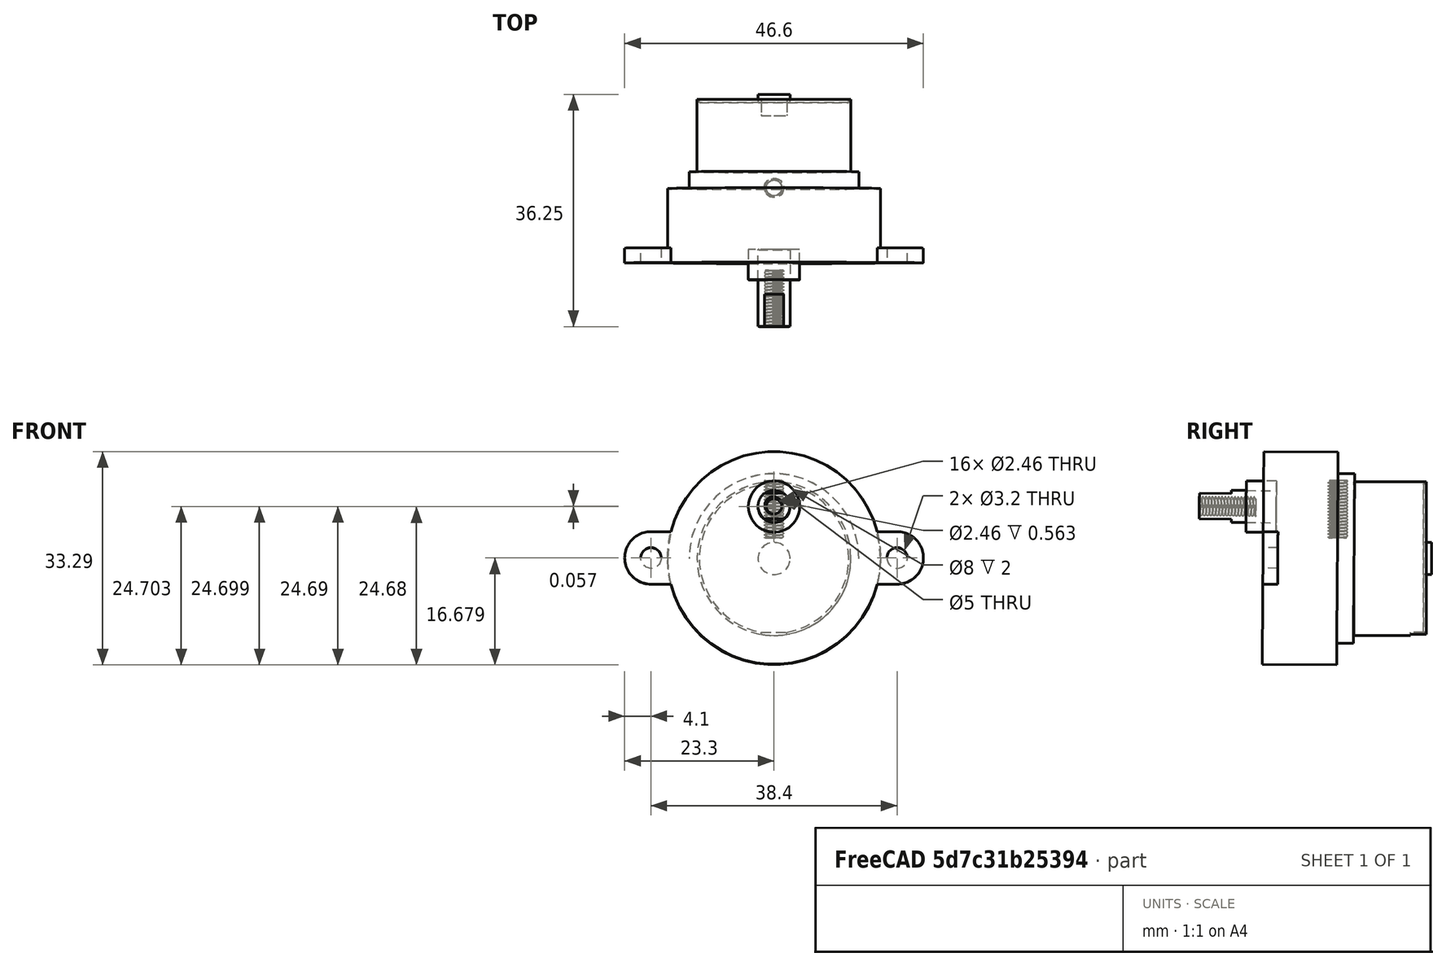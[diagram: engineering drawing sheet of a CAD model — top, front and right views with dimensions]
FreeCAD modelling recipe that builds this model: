
FCSTD DOCUMENT  (FreeCAD 1.0R39319 (Git))
Label: JS30
License: CC0 1.0 Universal
LicenseURL: https://creativecommons.org/publicdomain/zero/1.0/legalcode.txt
objects: Sketcher::SketchObject×11, PartDesign::Pad×6, PartDesign::Pocket×5, PartDesign::Body×4, App::FeaturePython×4, PartDesign::Mirrored×2, Part::FeaturePython×1, PartDesign::Boolean×1, Assembly::JointGroup×1, Assembly::AssemblyObject×1
note: 66 computed .brp shape members not serialized (recipe doc carries the construction recipe); baked Part::Feature solids carry a one-line shape summary decoded from their .brp

FEATURE [Sketcher::SketchObject] Sketch
  ArcFitTolerance = 1e-06
  AttachmentSupport = -> [XZ_Plane]
  FullyConstrained = true
  MakeInternals = false
  MapMode = 5
  Placement = pos=(0,0,0) rot=(1,0,0;1.5708rad)
  sketch-geometry (1):
    g0: Circle CenterX=0 CenterY=0 CenterZ=0 NormalX=0 NormalY=0 NormalZ=1 AngleXU=0 Radius=12
  constraints (2):
    c: Diameter(g0) = 24
    c: Coincident(g0,g-1)
FEATURE [PartDesign::Pad] Pad
  Direction = (0,-1,2e-16)
  Length = 11.3
  Length2 = 10
  Placement = pos=(0,0,0) rot=(1,0,0;1.5708rad)
  Profile = -> Sketch [Edge1]
  ReferenceAxis = -> Sketch [N_Axis]
  Refine = true
  Reversed = true
  Suppressed = false
  Type = 0
FEATURE [Sketcher::SketchObject] Sketch001
  ArcFitTolerance = 1e-06
  AttachmentSupport = -> [Pad]
  FullyConstrained = true
  MakeInternals = false
  MapMode = 5
  Placement = pos=(0,11.3,0) rot=(-1,0,0;1.5708rad)
  sketch-geometry (1):
    g0: Circle CenterX=0 CenterY=0 CenterZ=0 NormalX=0 NormalY=0 NormalZ=1 AngleXU=0 Radius=11.65
  constraints (2):
    c: Diameter(g0) = 23.3
    c: Coincident(g0,g-1)
FEATURE [PartDesign::Pocket] Pocket
  BaseFeature = -> Pad
  Direction = (0,-1,-2e-16)
  Length = 0.5
  Length2 = 5
  Placement = pos=(0,0,0) rot=(1,0,0;1.5708rad)
  Profile = -> Sketch001
  ReferenceAxis = -> Sketch001 [N_Axis]
  Refine = true
  Suppressed = false
  Type = 0
FEATURE [Sketcher::SketchObject] Sketch002
  ArcFitTolerance = 1e-06
  AttachmentSupport = -> [XZ_Plane001]
  FullyConstrained = true
  MakeInternals = false
  MapMode = 5
  Placement = pos=(0,0,0) rot=(1,0,0;1.5708rad)
  sketch-geometry (1):
    g0: Circle CenterX=0 CenterY=0 CenterZ=0 NormalX=0 NormalY=0 NormalZ=1 AngleXU=0 Radius=16.6
  constraints (2):
    c: Diameter(g0) = 33.2
    c: Coincident(g0,g-1)
FEATURE [PartDesign::Pad] Pad001
  Direction = (0,-1,2e-16)
  Length = 14.2
  Length2 = 10
  Placement = pos=(0,0,0) rot=(1,0,0;1.5708rad)
  Profile = -> Sketch002 [Edge1]
  ReferenceAxis = -> Sketch002 [N_Axis]
  Refine = true
  Suppressed = false
  Type = 0
FEATURE [Sketcher::SketchObject] Sketch003
  ArcFitTolerance = 1e-06
  AttachmentSupport = -> [XZ_Plane001]
  ExternalGeometry = -> [Pad001]
  FullyConstrained = true
  MakeInternals = false
  MapMode = 5
  Placement = pos=(0,0,0) rot=(1,0,0;1.5708rad)
  sketch-geometry (2):
    g0: Circle CenterX=0 CenterY=0 CenterZ=0 NormalX=0 NormalY=0 NormalZ=1 AngleXU=0 Radius=13.25
    g1: Circle CenterX=0 CenterY=0 CenterZ=0 NormalX=0 NormalY=0 NormalZ=1 AngleXU=0 Radius=16.6
  constraints (4):
    c: Diameter(g0) = 26.5
    c: Coincident(g0,g-1)
    c: Coincident(g1,g0)
    c: Equal(g1,g-3)
FEATURE [PartDesign::Pocket] Pocket001
  BaseFeature = -> Pad001
  Direction = (0,1,-2e-16)
  Length = 2.6
  Length2 = 5
  Placement = pos=(0,0,0) rot=(1,0,0;1.5708rad)
  Profile = -> Sketch003
  ReferenceAxis = -> Sketch003 [N_Axis]
  Refine = true
  Reversed = true
  Suppressed = false
  Type = 0
FEATURE [Sketcher::SketchObject] Sketch004
  ArcFitTolerance = 1e-06
  AttachmentSupport = -> [Pocket]
  ExternalGeometry = -> [Pocket]
  FullyConstrained = true
  MakeInternals = false
  MapMode = 5
  Placement = pos=(0,11.3,0) rot=(-1,0,0;1.5708rad)
  sketch-geometry (6):
    g0: GeomPoint X=0 Y=12 Z=0
    g1: LineSegment StartX=0 StartY=12 StartZ=0 EndX=2 EndY=12 EndZ=0
    g2: GeomPoint X=2 Y=11.477 Z=0
    g3: LineSegment StartX=2 StartY=12 StartZ=0 EndX=2 EndY=11.477 EndZ=0
    g4: LineSegment StartX=2 StartY=11.477 StartZ=0 EndX=0 EndY=11.477 EndZ=0
    g5: LineSegment StartX=0 StartY=11.477 StartZ=0 EndX=0 EndY=12 EndZ=0
  constraints (14):
    c: PointOnObject(g0,g-3)
    c: PointOnObject(g0,g-2)
    c: PointOnObject(g2,g-4)
    c: DistanceX(g1,g1) = 2
    c: Horizontal(g1,g1)
    c: Vertical(g1,g2)
    c: Coincident(g1,g0)
    c: Coincident(g3,g1)
    c: Coincident(g3,g2)
    c: Coincident(g4,g2)
    c: PointOnObject(g4,g-2)
    c: Horizontal(g4)
    c: Coincident(g5,g4)
    c: Coincident(g5,g0)
FEATURE [PartDesign::Pocket] Pocket002
  BaseFeature = -> Pocket
  Direction = (0,-1,-2e-16)
  Length = 2.5
  Length2 = 5
  Placement = pos=(0,0,0) rot=(1,0,0;1.5708rad)
  Profile = -> Sketch004
  ReferenceAxis = -> Sketch004 [N_Axis]
  Refine = true
  Suppressed = false
  Type = 0
FEATURE [Sketcher::SketchObject] Sketch005
  ArcFitTolerance = 1e-06
  AttachmentSupport = -> [Pocket001]
  FullyConstrained = true
  MakeInternals = false
  MapMode = 5
  Placement = pos=(0,-14.2,0) rot=(1,0,0;1.5708rad)
  sketch-geometry (14):
    g0: ArcOfCircle CenterX=19.2 CenterY=0 CenterZ=0 NormalX=0 NormalY=0 NormalZ=1 AngleXU=0 Radius=4.1 StartAngle=4.71239 EndAngle=7.85398
    g1: Circle CenterX=19.2 CenterY=0 CenterZ=0 NormalX=0 NormalY=0 NormalZ=1 AngleXU=0 Radius=1.6
    g2: LineSegment [constr] StartX=0 StartY=0 StartZ=0 EndX=9.6 EndY=0 EndZ=0
    g3: LineSegment [constr] StartX=9.6 StartY=0 StartZ=0 EndX=9.6 EndY=4.1 EndZ=0
    g4: LineSegment [constr] StartX=9.6 StartY=4.1 StartZ=0 EndX=0 EndY=4.1 EndZ=0
    g5: LineSegment [constr] StartX=0 StartY=4.1 StartZ=0 EndX=0 EndY=0 EndZ=0
    g6: LineSegment [constr] StartX=0 StartY=0 StartZ=0 EndX=0 EndY=-4.1 EndZ=0
    g7: LineSegment [constr] StartX=0 StartY=-4.1 StartZ=0 EndX=9.6 EndY=-4.1 EndZ=0
    g8: LineSegment [constr] StartX=9.6 StartY=-4.1 StartZ=0 EndX=9.6 EndY=0 EndZ=0
    g9: LineSegment [constr] StartX=9.6 StartY=0 StartZ=0 EndX=0 EndY=0 EndZ=0
    g10: LineSegment [constr] StartX=9.6 StartY=0 StartZ=0 EndX=19.2 EndY=0 EndZ=0
    g11: LineSegment StartX=9.6 StartY=4.1 StartZ=0 EndX=9.6 EndY=-4.1 EndZ=0
    g12: LineSegment StartX=9.6 StartY=-4.1 StartZ=0 EndX=19.2 EndY=-4.1 EndZ=0
    g13: LineSegment StartX=19.2 StartY=4.1 StartZ=0 EndX=9.6 EndY=4.1 EndZ=0
  constraints (38):
    c: Angle(g0) = 3.14159
    c: Diameter(g1) = 3.2
    c: Coincident(g1,g0)
    c: Coincident(g2,g3)
    c: Coincident(g3,g4)
    c: Coincident(g4,g5)
    c: Coincident(g5,g2)
    c: Horizontal(g2)
    c: Horizontal(g4)
    c: Vertical(g3)
    c: Vertical(g5)
    c: Coincident(g2,g-1)
    c: Coincident(g6,g7)
    c: Coincident(g7,g8)
    c: Coincident(g8,g9)
    c: Coincident(g9,g6)
    c: Vertical(g6)
    c: Vertical(g8)
    c: Horizontal(g7)
    c: Horizontal(g9)
    c: Coincident(g6,g2)
    c: Equal(g6,g5)
    c: Equal(g4,g7)
    c: PointOnObject(g0,g-1)
    c: Coincident(g10,g2)
    c: Coincident(g10,g0)
    c: Equal(g10,g2)
    c: DistanceX(g4,g0) = 19.2
    c: Coincident(g11,g12)
    c: Coincident(g13,g11)
    c: Vertical(g11)
    c: Horizontal(g12)
    c: Horizontal(g13)
    c: Coincident(g11,g3)
    c: Coincident(g12,g0)
    c: DistanceY(g0,g0) = 8.2
    c: Coincident(g13,g0)
    c: Vertical(g0,g0)
FEATURE [Sketcher::SketchObject] Sketch006
  ArcFitTolerance = 1e-06
  AttachmentSupport = -> [XZ_Plane002]
  FullyConstrained = true
  MakeInternals = false
  MapMode = 5
  Placement = pos=(0,0,0) rot=(1,0,0;1.5708rad)
  sketch-geometry (2):
    g0: Circle CenterX=0 CenterY=0 CenterZ=0 NormalX=0 NormalY=0 NormalZ=1 AngleXU=0 Radius=2.5
    g1: Circle CenterX=0 CenterY=0 CenterZ=0 NormalX=0 NormalY=0 NormalZ=1 AngleXU=0 Radius=4
  constraints (4):
    c: Diameter(g0) = 5
    c: Coincident(g0,g-1)
    c: Diameter(g1) = 8
    c: Coincident(g1,g0)
FEATURE [PartDesign::Pad] Pad003
  Direction = (0,-1,2e-16)
  Length = 4.7
  Length2 = 10
  Placement = pos=(0,0,0) rot=(1,0,0;1.5708rad)
  Profile = -> Sketch006
  ReferenceAxis = -> Sketch006 [N_Axis]
  Refine = true
  Suppressed = false
  Type = 0
FEATURE [PartDesign::Body] Body002  label="Brushing"
  AllowCompound = false
  Group = -> [Sketch006,Pad003]
  Origin = -> Origin002
  Placement = pos=(-6e-15,-12.1388,8.09249) rot=(-1,0,0;0.0076rad)
  Tip = -> Pad003
FEATURE [Sketcher::SketchObject] Sketch009
  ArcFitTolerance = 1e-06
  AttachmentSupport = -> [Pocket001]
  FullyConstrained = true
  MakeInternals = false
  MapMode = 5
  Placement = pos=(0,-14.2,0) rot=(1,0,0;1.5708rad)
  sketch-geometry (2):
    g0: LineSegment [constr] StartX=0 StartY=0 StartZ=0 EndX=0 EndY=8 EndZ=0
    g1: Circle CenterX=0 CenterY=8 CenterZ=0 NormalX=0 NormalY=0 NormalZ=1 AngleXU=0 Radius=4
  constraints (5):
    c: Distance(g0) = 8
    c: Coincident(g0,g-1)
    c: PointOnObject(g0,g-2)
    c: Diameter(g1) = 8
    c: Coincident(g1,g0)
FEATURE [PartDesign::Pocket] Pocket004
  BaseFeature = -> Pocket001
  Direction = (0,1,-2e-16)
  Length = 2
  Length2 = 5
  Placement = pos=(0,0,0) rot=(1,0,0;1.5708rad)
  Profile = -> Sketch009
  ReferenceAxis = -> Sketch009 [N_Axis]
  Refine = true
  Suppressed = false
  Type = 0
FEATURE [App::FeaturePython] Joint  label="FixedGearBox"  # Assembly joint (typed FeaturePython)
  Activated = true
  AngleMax = 0
  AngleMin = 0
  Detach1 = false
  Detach2 = false
  Distance = 0
  Distance2 = 0
  EnableAngleMax = false
  EnableAngleMin = false
  EnableLengthMax = false
  EnableLengthMin = false
  JointType = 0 (Fixed)
  LengthMax = 0
  LengthMin = 0
  Placement1 = pos=(2e-16,0,3e-16) rot=(0.57735,0.57735,0.57735;4.18879rad)
  Reference1 = -> Assembly [Body001.Face14,Body001.Face14]
  Reference2 = -> Assembly [Body.?Face6,Body.?Face6]
FEATURE [App::FeaturePython] Joint002  label="FixedBrushing"  # Assembly joint (typed FeaturePython)
  Activated = true
  AngleMax = 0
  AngleMin = 0
  Detach1 = false
  Detach2 = false
  Distance = 0
  Distance2 = 0
  EnableAngleMax = false
  EnableAngleMin = false
  EnableLengthMax = false
  EnableLengthMin = false
  JointType = 0 (Fixed)
  LengthMax = 0
  LengthMin = 0
  Placement1 = pos=(7.9e-15,-12.2,8) rot=(0.57735,0.57735,0.57735;4.18879rad)
  Placement2 = pos=(3.9e-15,0,0) rot=(0.57735,0.57735,0.57735;4.18879rad)
  Reference1 = -> Assembly [Body001.Face17,Body001.Face17]
  Reference2 = -> Assembly [Body002.Face3,Body002.Face3]
FEATURE [Sketcher::SketchObject] Sketch010
  ArcFitTolerance = 1e-06
  AttachmentSupport = -> [XY_Plane005]
  FullyConstrained = true
  MakeInternals = false
  MapMode = 5
  sketch-geometry (1):
    g0: Circle CenterX=0 CenterY=-2.5 CenterZ=0 NormalX=0 NormalY=0 NormalZ=1 AngleXU=0 Radius=2.5
  constraints (3):
    c: Diameter(g0) = 5
    c: PointOnObject(g0,g-2)
    c: Tangent(g0,g-1)
FEATURE [PartDesign::Pad] Pad004
  Direction = (0,0,1)
  Length = 12
  Length2 = 10
  Profile = -> Sketch010
  ReferenceAxis = -> Sketch010 [N_Axis]
  Refine = true
  Suppressed = false
  Type = 0
FEATURE [Part::FeaturePython] ScrewTap  label="M3x9-ScrewTap"  # WARN: FeaturePython — macro-defined, semantics opaque (R4)
  Diameter = 4
  DiameterCustom = 6
  Invert = false
  LeftHanded = false
  Length = 9
  MatchOuter = false
  OffsetAngle = 0
  PitchCustom = 1
  Placement = pos=(0,-2.5,12.2) rot=(0,0,1;0rad)
  Thread = true
  Type = 2
FEATURE [PartDesign::Boolean] Boolean
  BaseFeature = -> Pad004
  Group = -> [ScrewTap]
  Placement = pos=(0,2.5,0) rot=(0,0,1;0rad)
  Refine = true
  Suppressed = false
  Type = 1
  UsePlacement = true
FEATURE [Sketcher::SketchObject] Sketch011
  ArcFitTolerance = 1e-06
  AttachmentSupport = -> [Boolean]
  FullyConstrained = true
  MakeInternals = false
  MapMode = 5
  Placement = pos=(0,2.5,12) rot=(0,0,1;0rad)
  sketch-geometry (14):
    g0: GeomPoint [constr] X=0 Y=-2.5 Z=0
    g1: LineSegment [constr] StartX=-2 StartY=-5 StartZ=0 EndX=2 EndY=-5 EndZ=0
    g2: LineSegment [constr] StartX=2 StartY=-5 StartZ=0 EndX=2 EndY=0 EndZ=0
    g3: LineSegment [constr] StartX=2 StartY=0 StartZ=0 EndX=-2 EndY=0 EndZ=0
    g4: LineSegment [constr] StartX=-2 StartY=0 StartZ=0 EndX=-2 EndY=-5 EndZ=0
    g5: GeomPoint [constr] X=0 Y=-2.5 Z=0
    g6: LineSegment StartX=-3 StartY=0 StartZ=0 EndX=-3 EndY=-5 EndZ=0
    g7: LineSegment StartX=-3 StartY=-5 StartZ=0 EndX=-2 EndY=-5 EndZ=0
    g8: LineSegment StartX=-2 StartY=-5 StartZ=0 EndX=-2 EndY=0 EndZ=0
    g9: LineSegment StartX=-2 StartY=0 StartZ=0 EndX=-3 EndY=0 EndZ=0
    g10: LineSegment StartX=2 StartY=0 StartZ=0 EndX=3 EndY=0 EndZ=0
    g11: LineSegment StartX=3 StartY=0 StartZ=0 EndX=3 EndY=-5 EndZ=0
    g12: LineSegment StartX=2 StartY=-5 StartZ=0 EndX=2 EndY=0 EndZ=0
    g13: LineSegment StartX=3 StartY=-5 StartZ=0 EndX=2 EndY=-5 EndZ=0
  constraints (36):
    c: PointOnObject(g0,g-2)
    c: Coincident(g1,g2)
    c: Coincident(g2,g3)
    c: Coincident(g3,g4)
    c: Coincident(g4,g1)
    c: Horizontal(g1)
    c: Horizontal(g3)
    c: Vertical(g2)
    c: Vertical(g4)
    c: Symmetric(g3,g1,g5)
    c: Distance(g2,g4) = 4
    c: Distance(g1,g3) = 5
    c: Coincident(g5,g0)
    c: PointOnObject(g2,g-1)
    c: Coincident(g6,g7)
    c: Coincident(g7,g8)
    c: Coincident(g8,g9)
    c: Coincident(g9,g6)
    c: Vertical(g6)
    c: Vertical(g8)
    c: Horizontal(g7)
    c: Horizontal(g9)
    c: DistanceX(g9,g9) = 1
    c: Equal(g2,g6)
    c: Coincident(g8,g3)
    c: Coincident(g11,g13)
    c: Coincident(g13,g12)
    c: Coincident(g12,g10)
    c: Coincident(g10,g11)
    c: Vertical(g11)
    c: Vertical(g12)
    c: Horizontal(g13)
    c: Horizontal(g10)
    c: Equal(g10,g9)
    c: Equal(g6,g11)
    c: Coincident(g2,g10)
FEATURE [PartDesign::Pocket] Pocket005
  BaseFeature = -> Boolean
  Direction = (0,0,-1)
  Length = 5
  Length2 = 5
  Placement = pos=(0,2.5,0) rot=(0,0,1;0rad)
  Profile = -> Sketch011
  ReferenceAxis = -> Sketch011 [N_Axis]
  Refine = true
  Suppressed = false
  Type = 0
FEATURE [PartDesign::Body] Body003  label="Shaft"
  AllowCompound = false
  Group = -> [Sketch010,Pad004,Boolean,Sketch011,Pocket005]
  Origin = -> Origin005
  Placement = pos=(-2.4e-15,-12.1388,8.09249) rot=(0.576856,-0.575398,0.579788;2.08854rad)
  Tip = -> Pocket005
FEATURE [App::FeaturePython] Joint003  label="RevoluteShaft"  # Assembly joint (typed FeaturePython)
  Activated = true
  AngleMax = 0
  AngleMin = 0
  Detach1 = false
  Detach2 = false
  Distance = 0
  Distance2 = 0
  EnableAngleMax = false
  EnableAngleMin = false
  EnableLengthMax = false
  EnableLengthMin = false
  JointType = 1 (Revolute)
  LengthMax = 0
  LengthMin = 0
  Placement1 = pos=(7.9e-15,-12.2,8) rot=(0.57735,0.57735,0.57735;4.18879rad)
  Placement2 = pos=(-1.8e-15,-3e-16,0) rot=(0,0,1;0rad)
  Reference1 = -> Assembly [Body001.Face17,Body001.Face17]
  Reference2 = -> Assembly [Body003.Face2,Body003.Face2]
FEATURE [PartDesign::Pad] Pad005
  BaseFeature = -> Pocket004
  Direction = (0,-1,2e-16)
  Length = 2.3
  Length2 = 10
  Placement = pos=(0,0,0) rot=(1,0,0;1.5708rad)
  Profile = -> Sketch005
  ReferenceAxis = -> Sketch005 [N_Axis]
  Refine = true
  Reversed = true
  Suppressed = false
  Type = 0
FEATURE [PartDesign::Mirrored] Mirrored
  BaseFeature = -> Pad005
  MirrorPlane = -> Sketch005 [V_Axis]
  Originals = -> [Pad005]
  Placement = pos=(0,0,0) rot=(1,0,0;1.5708rad)
  Refine = true
  Suppressed = false
  TransformMode = 0
FEATURE [PartDesign::Body] Body001  label="GearBox"
  AllowCompound = false
  Group = -> [Sketch002,Pad001,Sketch003,Pocket001,Sketch005,Sketch009,Pocket004,Pad005,Mirrored]
  Origin = -> Origin001
  Placement = pos=(-2e-16,0,-3e-16) rot=(-1,0,0;0.0076rad)
  Tip = -> Mirrored
FEATURE [PartDesign::Mirrored] Mirrored001
  BaseFeature = -> Pocket002
  MirrorPlane = -> Sketch004 [V_Axis]
  Originals = -> [Pocket002]
  Placement = pos=(0,0,0) rot=(1,0,0;1.5708rad)
  Refine = true
  Suppressed = false
  TransformMode = 0
FEATURE [Sketcher::SketchObject] Sketch012
  ArcFitTolerance = 1e-06
  AttachmentSupport = -> [Pocket]
  FullyConstrained = true
  MakeInternals = false
  MapMode = 5
  Placement = pos=(0,10.8,0) rot=(-1,0,0;1.5708rad)
  sketch-geometry (1):
    g0: Circle CenterX=0 CenterY=0 CenterZ=0 NormalX=0 NormalY=0 NormalZ=1 AngleXU=0 Radius=2.5
  constraints (2):
    c: Diameter(g0) = 5
    c: Coincident(g0,g-1)
FEATURE [PartDesign::Pad] Pad006
  BaseFeature = -> Mirrored001
  Direction = (0,1,2e-16)
  Length = 1.3
  Length2 = 10
  Placement = pos=(0,0,0) rot=(1,0,0;1.5708rad)
  Profile = -> Sketch012 [Edge1]
  ReferenceAxis = -> Sketch012 [N_Axis]
  Refine = true
  Suppressed = false
  Type = 0
FEATURE [PartDesign::Body] Body  label="Motor"
  AllowCompound = false
  Group = -> [Sketch,Pad,Sketch001,Pocket,Sketch004,Pocket002,Mirrored001,Sketch012,Pad006]
  Origin = -> Origin
  Tip = -> Pad006
FEATURE [App::FeaturePython] GroundedJoint  # Assembly grounded joint (typed FeaturePython)
  ObjectToGround = -> Body
FEATURE [Assembly::JointGroup] Joints
  Group = -> [GroundedJoint,Joint,Joint002,Joint003]
FEATURE [Assembly::AssemblyObject] Assembly
  Group = -> [Joints,Body,Body001,Body002,GroundedJoint,Joint,Joint002,Body003,Joint003]
  Origin = -> Origin004
  Type = Assembly
